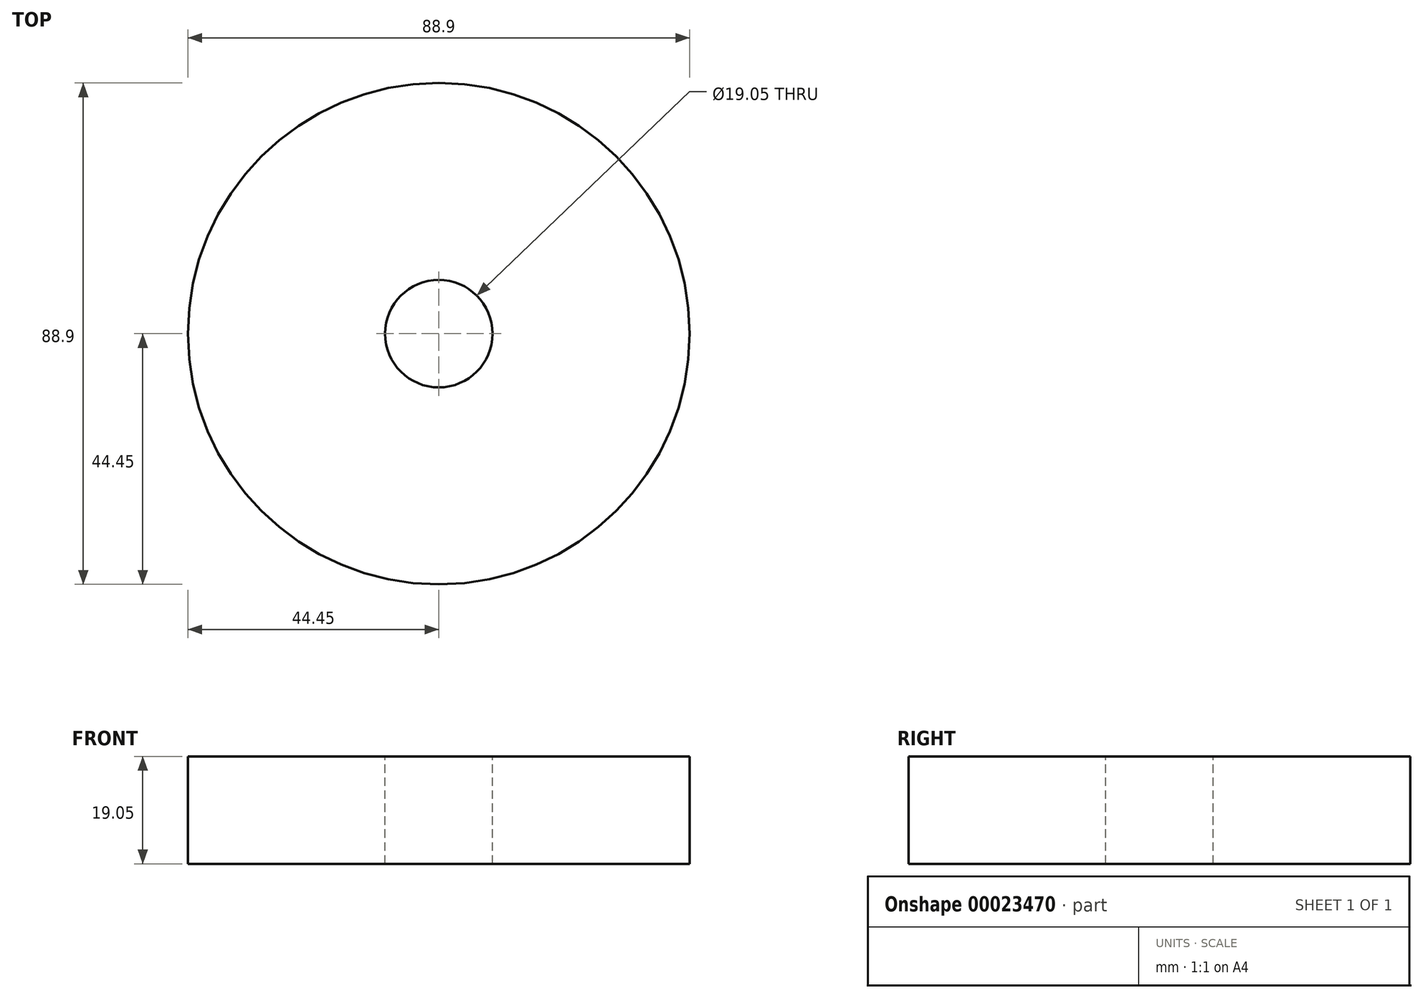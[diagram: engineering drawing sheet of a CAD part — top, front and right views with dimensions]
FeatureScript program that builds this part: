
annotation { "Feature Type Name" : "Feature", "Feature Type Description" : "" }
export const myFeature = defineFeature(function(context is Context, id is Id, definition is map)
    precondition{}
    {
        {
            var Q0;
            Q0=qCreatedBy(makeId("Front.planeOp"),FACE);
            var sketch = newSketch(context, id + "F0", { "sketchPlane" : qUnion([Q0])});
            skLineSegment(sketch, "E0", {"start": v(0, 44.2) * mm, "end": v(0, -52.26) * mm, "construction": true});
            skLineSegment(sketch, "E1", {"start": v(0, 0) * mm, "end": v(-9.52, 0) * mm});
            skLineSegment(sketch, "E2", {"start": v(-9.52, 35.67) * mm, "end": v(-9.52, -43.55) * mm, "construction": true});
            skLineSegment(sketch, "E3.bottom", {"start": v(-9.52, -43.55) * mm, "end": v(-44.45, -43.55) * mm});
            skLineSegment(sketch, "E3.top", {"start": v(-9.52, -24.5) * mm, "end": v(-44.45, -24.5) * mm});
            skLineSegment(sketch, "E3.left", {"start": v(-9.52, -43.55) * mm, "end": v(-9.52, -24.5) * mm});
            skLineSegment(sketch, "E3.right", {"start": v(-44.45, -43.55) * mm, "end": v(-44.45, -24.5) * mm});
            skLineSegment(sketch, "E4.bottom", {"start": v(-9.52, -24.5) * mm, "end": v(-25.4, -24.5) * mm});
            skLineSegment(sketch, "E4.top", {"start": v(-9.52, 32.65) * mm, "end": v(-25.4, 32.65) * mm});
            skLineSegment(sketch, "E4.left", {"start": v(-9.52, -24.5) * mm, "end": v(-9.52, 32.65) * mm});
            skLineSegment(sketch, "E4.right", {"start": v(-25.4, -24.5) * mm, "end": v(-25.4, 32.65) * mm});
            skLineSegment(sketch, "E5.bottom", {"start": v(-9.52, 32.65) * mm, "end": v(-19.05, 32.65) * mm});
            skLineSegment(sketch, "E5.top", {"start": v(-9.53, 45.35) * mm, "end": v(-19.05, 45.35) * mm});
            skLineSegment(sketch, "E5.left", {"start": v(-9.53, 32.65) * mm, "end": v(-9.53, 45.35) * mm});
            skLineSegment(sketch, "E5.right", {"start": v(-19.05, 32.65) * mm, "end": v(-19.05, 45.35) * mm});
            skSolve(sketch);
        }
        {
            var Q0;
            Q0=makeQuery(id+"F0.imprint","IMPRINT",FACE,{"disambiguationData":[TD([[makeQuery(id+"F0.imprint","IMPRINT",EDGE,{"derivedFrom":sQuery(id+"F0.wireOp",EDGE,"E3.bottom")}),-1.0]])]});
            var Q1;
            {var subQ3=sQuery(id+"F0.wireOp",EDGE,"E4.bottom");Q1=makeQuery(id+"F0.imprint","IMPRINT",FACE,{"disambiguationData":[TD([[makeQuery(id+"F0.imprint","IMPRINT",EDGE,{"derivedFrom":subQ3}),-1.0]])]});}
            var Q2;
            Q2=makeQuery(id+"F0.imprint","IMPRINT",FACE,{"disambiguationData":[TD([[makeQuery(id+"F0.imprint","IMPRINT",EDGE,{"derivedFrom":sQuery(id+"F0.wireOp",EDGE,"E5.bottom")}),-1.0]])]});
            var Q3;
            Q3=sQuery(id+"F0.wireOp",EDGE,"E0");
            revolve(context, id + "F1", {"entities" : qUnion([Q0, Q1, Q2]), "axis" : qUnion([Q3]), "revolveType" : RevolveType.FULL});
        }
    });
